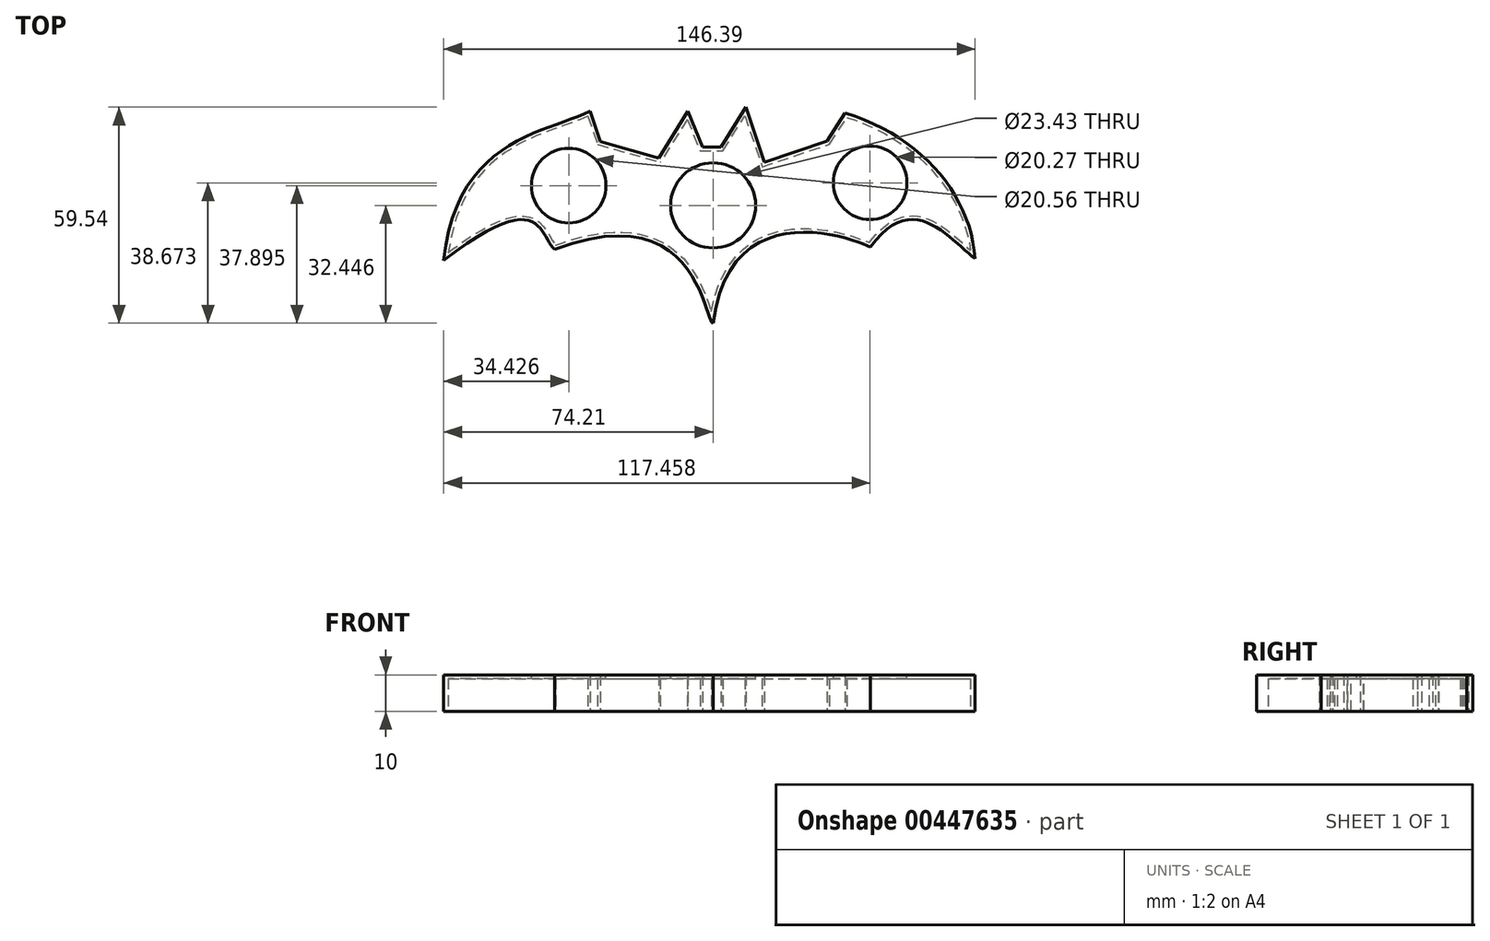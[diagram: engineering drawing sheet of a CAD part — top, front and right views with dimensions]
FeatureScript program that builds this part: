
annotation { "Feature Type Name" : "Feature", "Feature Type Description" : "" }
export const myFeature = defineFeature(function(context is Context, id is Id, definition is map)
    precondition{}
    {
        {
            var Q0;
            Q0=qCreatedBy(makeId("Top.planeOp"),FACE);
            var sketch = newSketch(context, id + "F0", { "sketchPlane" : qUnion([Q0])});
            skLineSegment(sketch, "E0", {"start": v(-33.94, 22.96) * mm, "end": v(-31.08, 14.66) * mm});
            skLineSegment(sketch, "E1", {"start": v(-31.08, 14.66) * mm, "end": v(-15, 10.06) * mm});
            skLineSegment(sketch, "E2", {"start": v(-6.93, 22.96) * mm, "end": v(-15, 10.06) * mm});
            skLineSegment(sketch, "E3", {"start": v(-6.93, 22.96) * mm, "end": v(-2.91, 13.1) * mm});
            skFitSpline(sketch, "E4", {"points": [v(-2.91, 13.1) * mm, v(2.13, 13.1) * mm], "startDerivative": vector(4.67, 0) * mm, "endDerivative": vector(4.67, 0) * mm});
            skLineSegment(sketch, "E5", {"start": v(2.13, 13.1) * mm, "end": v(9.06, 24.1) * mm});
            skLineSegment(sketch, "E6", {"start": v(9.06, 24.1) * mm, "end": v(14.15, 8.93) * mm});
            skLineSegment(sketch, "E7", {"start": v(14.15, 8.93) * mm, "end": v(31.38, 14.72) * mm});
            skLineSegment(sketch, "E8", {"start": v(31.38, 14.72) * mm, "end": v(36.39, 22.45) * mm});
            skFitSpline(sketch, "E9", {"points": [v(36.39, 22.45) * mm, v(72.18, -17.65) * mm], "startDerivative": vector(63.18, -19.35) * mm, "endDerivative": vector(3.79, -52.96) * mm});
            skFitSpline(sketch, "E10", {"points": [v(-33.94, 22.96) * mm, v(-74.21, -18.19) * mm], "startDerivative": vector(-35.8, -17.9) * mm, "endDerivative": vector(-10.45, -101.5) * mm});
            skFitSpline(sketch, "E11", {"points": [v(-74.21, -18.19) * mm, v(-43.67, -15.14) * mm], "startDerivative": vector(81.17, 63.02) * mm, "endDerivative": vector(12.63, -11.88) * mm});
            skFitSpline(sketch, "E12", {"points": [v(-43.67, -15.14) * mm, v(0, -35.43) * mm], "startDerivative": vector(119.8, 45.4) * mm, "endDerivative": vector(7.64, 0) * mm});
            skFitSpline(sketch, "E13", {"points": [v(0, -35.43) * mm, v(43.37, -14.51) * mm], "startDerivative": vector(13.51, 106.3) * mm, "endDerivative": vector(17.13, -8.56) * mm});
            skFitSpline(sketch, "E14", {"points": [v(43.37, -14.51) * mm, v(72.18, -17.65) * mm], "startDerivative": vector(35.16, 49.75) * mm, "endDerivative": vector(20.23, -14.82) * mm});
            skSolve(sketch);
        }
        {
            var Q0;
            Q0 = qSketchRegion(id + "F3", true);
            var Q1;
            Q1 = qSketchRegion(id + "F0", true);
            extrude(context, id + "F1", {"entities" : qUnion([Q0, Q1]), "depth" : 10 * mm});
        }
        {
            var Q0;
            Q0=makeQuery(id+"F1.opExtrude","CAP_FACE",FACE,{"disambiguationData":[OSD([sQuery(id+"F0.wireOp",EDGE,"E0"),sQuery(id+"F0.wireOp",EDGE,"E1"),sQuery(id+"F0.wireOp",EDGE,"E2"),sQuery(id+"F0.wireOp",EDGE,"E3"),sQuery(id+"F0.wireOp",EDGE,"E4"),sQuery(id+"F0.wireOp",EDGE,"E5"),sQuery(id+"F0.wireOp",EDGE,"E6"),sQuery(id+"F0.wireOp",EDGE,"E7"),sQuery(id+"F0.wireOp",EDGE,"E8"),sQuery(id+"F0.wireOp",EDGE,"E9"),sQuery(id+"F0.wireOp",EDGE,"E10"),sQuery(id+"F0.wireOp",EDGE,"E11"),sQuery(id+"F0.wireOp",EDGE,"E12"),sQuery(id+"F0.wireOp",EDGE,"E13"),sQuery(id+"F0.wireOp",EDGE,"E14")])],"isStart":true});
            shell(context, id + "F2", {"entities" : qUnion([Q0]), "thickness" : 1 * mm});
        }
        {
            var Q0;
            Q0=makeQuery(id+"F1.opExtrude","CAP_FACE",FACE,{"disambiguationData":[OSD([sQuery(id+"F0.wireOp",EDGE,"E0"),sQuery(id+"F0.wireOp",EDGE,"E1"),sQuery(id+"F0.wireOp",EDGE,"E2"),sQuery(id+"F0.wireOp",EDGE,"E3"),sQuery(id+"F0.wireOp",EDGE,"E4"),sQuery(id+"F0.wireOp",EDGE,"E5"),sQuery(id+"F0.wireOp",EDGE,"E6"),sQuery(id+"F0.wireOp",EDGE,"E7"),sQuery(id+"F0.wireOp",EDGE,"E8"),sQuery(id+"F0.wireOp",EDGE,"E9"),sQuery(id+"F0.wireOp",EDGE,"E10"),sQuery(id+"F0.wireOp",EDGE,"E11"),sQuery(id+"F0.wireOp",EDGE,"E12"),sQuery(id+"F0.wireOp",EDGE,"E13"),sQuery(id+"F0.wireOp",EDGE,"E14")])],"isStart":false});
            var sketch = newSketch(context, id + "F3", { "sketchPlane" : qUnion([Q0])});
            skCircle(sketch, "E15", {"center": v(-39.78, 2.46) * mm, "radius": 10.28 * mm});
            skCircle(sketch, "E16", {"center": v(43.25, 3.24) * mm, "radius": 10.13 * mm});
            skCircle(sketch, "E17", {"center": v(0, -2.98) * mm, "radius": 11.72 * mm});
            skSolve(sketch);
        }
        {
            var Q0;
            Q0 = qSketchRegion(id + "F3", true);
            extrude(context, id + "F4", {"entities" : qUnion([Q0]), "operationType" : NewBodyOperationType.REMOVE, "oppositeDirection" : true, "depth" : 25 * mm});
        }
    });
